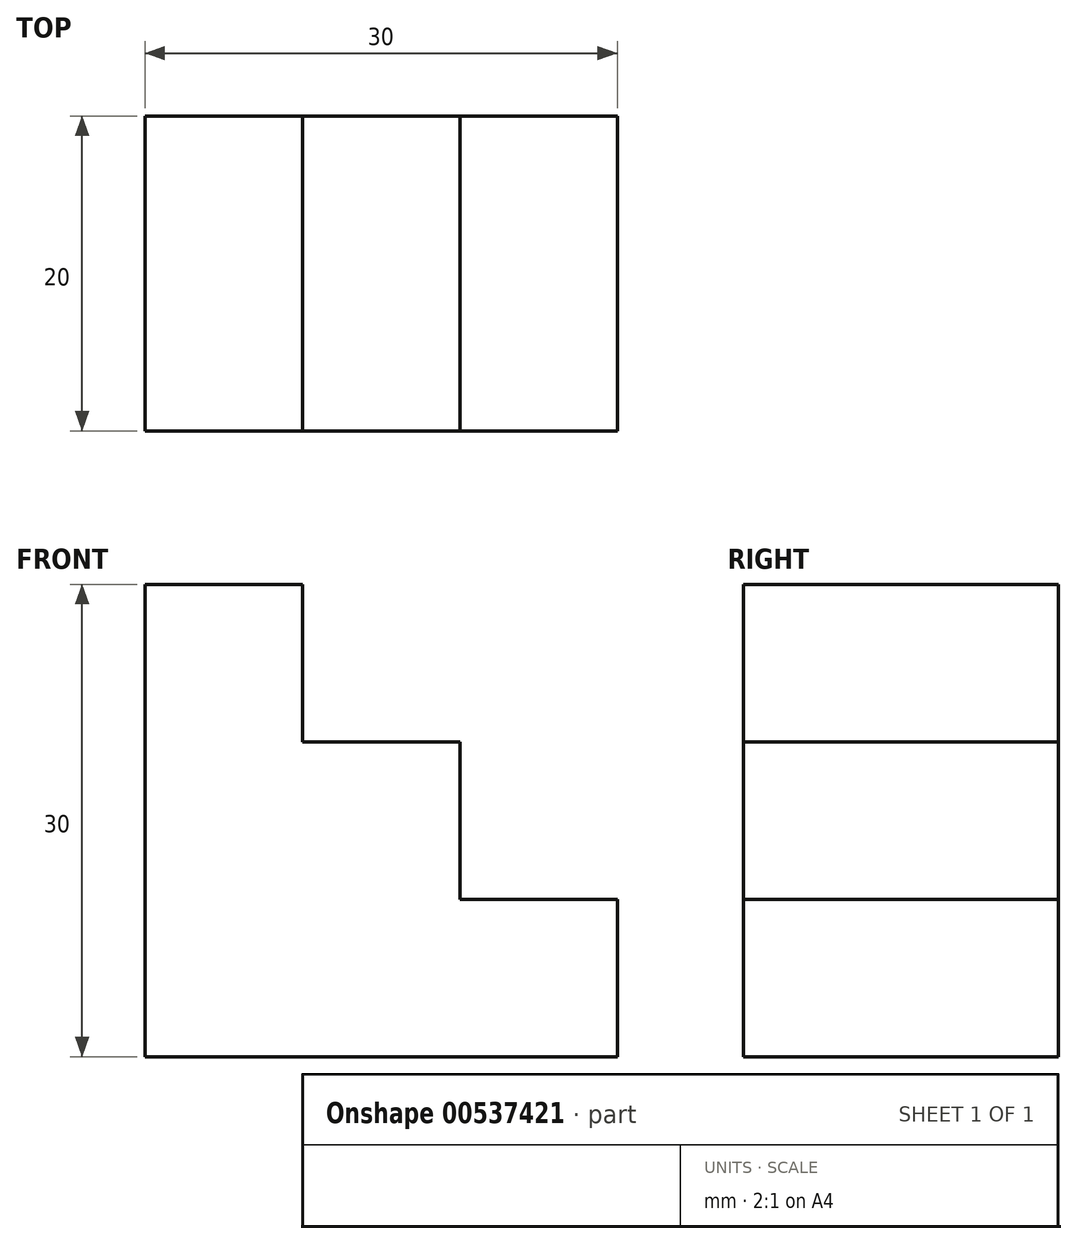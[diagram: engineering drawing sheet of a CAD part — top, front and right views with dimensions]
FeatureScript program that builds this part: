
annotation { "Feature Type Name" : "Feature", "Feature Type Description" : "" }
export const myFeature = defineFeature(function(context is Context, id is Id, definition is map)
    precondition{}
    {
        {
            var Q0;
            Q0=qCreatedBy(makeId("Top.planeOp"),FACE);
            var sketch = newSketch(context, id + "F0", { "sketchPlane" : qUnion([Q0])});
            skLineSegment(sketch, "E0.bottom", {"start": v(-36.36, -12.2) * mm, "end": v(-6.36, -12.2) * mm});
            skLineSegment(sketch, "E0.top", {"start": v(-36.36, 7.8) * mm, "end": v(-6.36, 7.8) * mm});
            skLineSegment(sketch, "E0.left", {"start": v(-36.36, -12.2) * mm, "end": v(-36.36, 7.8) * mm});
            skLineSegment(sketch, "E0.right", {"start": v(-6.36, -12.2) * mm, "end": v(-6.36, 7.8) * mm});
            skSolve(sketch);
        }
        {
            var Q0;
            Q0=makeQuery(id+"F0.imprint","IMPRINT",FACE,{"disambiguationData":[TD([[makeQuery(id+"F0.imprint","IMPRINT",EDGE,{"derivedFrom":sQuery(id+"F0.wireOp",EDGE,"E0.bottom")}),1.0]])]});
            extrude(context, id + "F1", {"entities" : qUnion([Q0]), "depth" : 30 * mm, "offsetDistance" : 25 * mm});
        }
        {
            var Q0;
            Q0=makeQuery(id+"F1.opExtrude","SWEPT_FACE",FACE,{"disambiguationData":[OSD([sQuery(id+"F0.wireOp",EDGE,"E0.bottom")])]});
            var sketch = newSketch(context, id + "F2", { "sketchPlane" : qUnion([Q0])});
            skLineSegment(sketch, "E1", {"start": v(-36.36, 30) * mm, "end": v(-26.36, 30) * mm});
            skLineSegment(sketch, "E2", {"start": v(-26.36, 30) * mm, "end": v(-26.36, 20) * mm});
            skLineSegment(sketch, "E3", {"start": v(-26.36, 20) * mm, "end": v(-16.36, 20) * mm});
            skLineSegment(sketch, "E4", {"start": v(-16.36, 20) * mm, "end": v(-16.36, 10) * mm});
            skLineSegment(sketch, "E5", {"start": v(-16.36, 10) * mm, "end": v(-6.36, 10) * mm});
            skLineSegment(sketch, "E6", {"start": v(-6.36, 10) * mm, "end": v(-6.36, 0) * mm});
            skSolve(sketch);
        }
        {
            var Q0;
            {var subQ1=sQuery(id+"F2.wireOp",EDGE,"E2");Q0=makeQuery(id+"F2.imprint","IMPRINT",FACE,{"disambiguationData":[TD([[makeQuery(id+"F2.imprint","IMPRINT",EDGE,{"derivedFrom":subQ1}),1.0]])]});}
            extrude(context, id + "F3", {"entities" : qUnion([Q0]), "operationType" : NewBodyOperationType.REMOVE, "endBound" : BoundingType.THROUGH_ALL, "oppositeDirection" : true, "depth" : 25 * mm, "offsetDistance" : 25 * mm});
        }
    });
